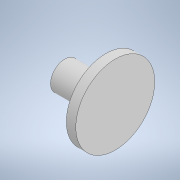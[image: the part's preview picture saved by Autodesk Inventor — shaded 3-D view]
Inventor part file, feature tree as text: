
AUTODESK INVENTOR PART (.ipt)
format: ipt  version: 2020 (Build 240168000, 168)  size: 105,472 bytes
history: native  units: in
note: dims shown in document units (in); Inventor stores cm internally (conversion verified against a paired STEP export)
features: extrude x2, sketch x2
ambient origin geometry x8: Origin, YZ Plane, XZ Plane, XY Plane, X Axis, Y Axis, Z Axis, Center Point
bodies: Solid1 (feature_tree)
feature tree (4):
  extrude  "Extrusion1"  Depth=0.1181in
  extrude  "Extrusion2"  Depth=0.5118in
  sketch  "Sketch1"  dims[d0=0.9843in d1=0.1181in]
  sketch  "Sketch2"  dims[d2=0.0in d3=0.3543in d4=0.5118in d5=0.0in]
